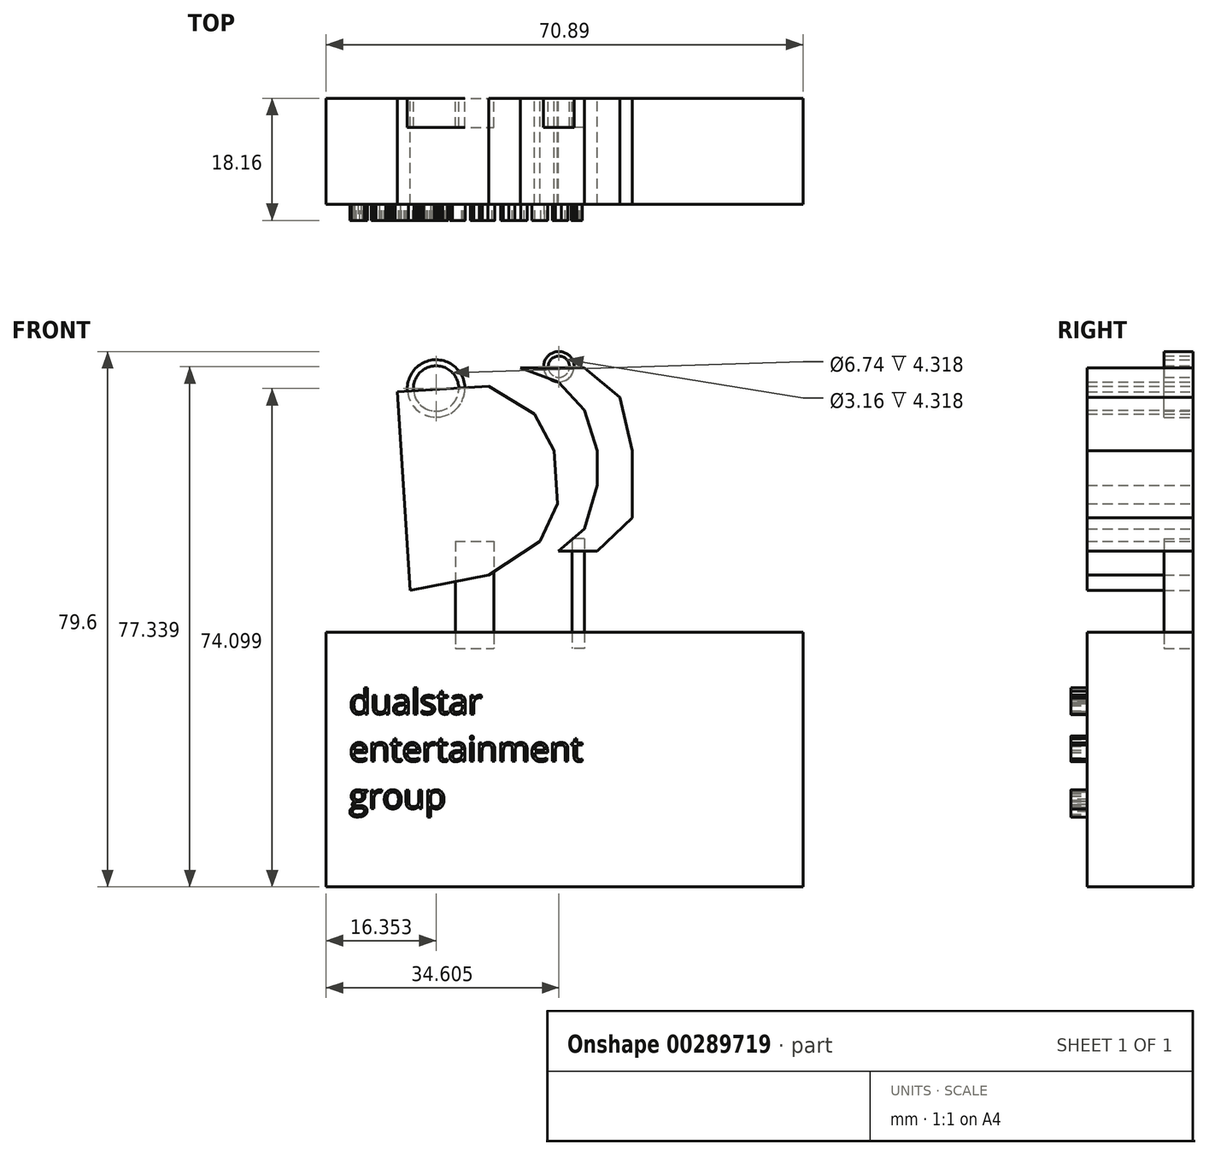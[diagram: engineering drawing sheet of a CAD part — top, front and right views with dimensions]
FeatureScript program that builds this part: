
annotation { "Feature Type Name" : "Feature", "Feature Type Description" : "" }
export const myFeature = defineFeature(function(context is Context, id is Id, definition is map)
    precondition{}
    {
        {
            var Q0;
            Q0=qCreatedBy(makeId("Front.planeOp"),FACE);
            var sketch = newSketch(context, id + "F0", { "sketchPlane" : qUnion([Q0])});
            skLineSegment(sketch, "E0", {"start": v(-25.92, 18.4) * mm, "end": v(-27.8, 47.92) * mm});
            skLineSegment(sketch, "E1", {"start": v(-27.8, 47.92) * mm, "end": v(-14.21, 48.78) * mm});
            skLineSegment(sketch, "E2", {"start": v(-14.21, 48.78) * mm, "end": v(-7.42, 44.6) * mm});
            skLineSegment(sketch, "E3", {"start": v(-7.42, 44.6) * mm, "end": v(-4.5, 39.19) * mm});
            skLineSegment(sketch, "E4", {"start": v(-4.5, 39.19) * mm, "end": v(-4, 31.28) * mm});
            skLineSegment(sketch, "E5", {"start": v(-4, 31.28) * mm, "end": v(-6.59, 25.67) * mm});
            skLineSegment(sketch, "E6", {"start": v(-6.59, 25.67) * mm, "end": v(-14.21, 20.69) * mm});
            skLineSegment(sketch, "E7", {"start": v(-14.21, 20.69) * mm, "end": v(-25.92, 18.4) * mm});
            skLineSegment(sketch, "E8", {"start": v(-9.5, 51.45) * mm, "end": v(-3.88, 49.37) * mm});
            skLineSegment(sketch, "E9", {"start": v(-3.88, 49.37) * mm, "end": v(0, 45.22) * mm});
            skLineSegment(sketch, "E10", {"start": v(0, 45.22) * mm, "end": v(1.94, 39.19) * mm});
            skLineSegment(sketch, "E11", {"start": v(1.94, 39.19) * mm, "end": v(1.94, 34) * mm});
            skLineSegment(sketch, "E12", {"start": v(1.94, 34) * mm, "end": v(0, 27.55) * mm});
            skLineSegment(sketch, "E13", {"start": v(0, 27.55) * mm, "end": v(-3.88, 24.22) * mm});
            skLineSegment(sketch, "E14", {"start": v(-3.88, 24.22) * mm, "end": v(1.94, 24.22) * mm});
            skLineSegment(sketch, "E15", {"start": v(1.94, 24.22) * mm, "end": v(7.14, 29.2) * mm});
            skLineSegment(sketch, "E16", {"start": v(7.14, 29.2) * mm, "end": v(7.14, 34) * mm});
            skLineSegment(sketch, "E17", {"start": v(7.14, 34) * mm, "end": v(7.14, 39.19) * mm});
            skLineSegment(sketch, "E18", {"start": v(7.14, 39.19) * mm, "end": v(5.26, 47.09) * mm});
            skLineSegment(sketch, "E19", {"start": v(5.26, 47.09) * mm, "end": v(0, 51.45) * mm});
            skLineSegment(sketch, "E20", {"start": v(0, 51.45) * mm, "end": v(-9.5, 51.45) * mm});
            skLineSegment(sketch, "E21.bottom", {"start": v(-38.4, 12.16) * mm, "end": v(32.5, 12.16) * mm});
            skLineSegment(sketch, "E21.top", {"start": v(-38.4, -25.68) * mm, "end": v(32.5, -25.68) * mm});
            skLineSegment(sketch, "E21.left", {"start": v(-38.4, 12.16) * mm, "end": v(-38.4, -25.68) * mm});
            skLineSegment(sketch, "E21.right", {"start": v(32.5, 12.16) * mm, "end": v(32.5, -25.68) * mm});
            skSolve(sketch);
        }
        {
            var Q0;
            Q0 = qSketchRegion(id + "F0", true);
            extrude(context, id + "F1", {"entities" : qUnion([Q0]), "depth" : 15.75 * mm});
        }
        {
            var Q0;
            Q0=qCreatedBy(makeId("Front.planeOp"),FACE);
            var sketch = newSketch(context, id + "F2", { "sketchPlane" : qUnion([Q0])});
            skText(sketch, "E22", { "text": "dualstar\nentertainment\ngroup\n", "fontName": "OpenSans-Regular.ttf"});
            const initialGuessF2  = {"E22": [-0.03497, 0, 1, 0, 0.00372]};
            skSetInitialGuess(sketch, initialGuessF2);
            skSolve(sketch);
        }
        {
            var Q0;
            Q0 = qSketchRegion(id + "F2", true);
            extrude(context, id + "F3", {"entities" : qUnion([Q0]), "operationType" : NewBodyOperationType.ADD, "depth" : 18.16 * mm});
        }
        {
            var Q0;
            Q0=qCreatedBy(makeId("Front.planeOp"),FACE);
            var sketch = newSketch(context, id + "F4", { "sketchPlane" : qUnion([Q0])});
            skLineSegment(sketch, "E23.bottom", {"start": v(-19.17, 25.7) * mm, "end": v(-13.46, 25.7) * mm});
            skLineSegment(sketch, "E23.top", {"start": v(-19.17, 9.74) * mm, "end": v(-13.46, 9.74) * mm});
            skLineSegment(sketch, "E23.left", {"start": v(-19.17, 25.7) * mm, "end": v(-19.17, 9.74) * mm});
            skLineSegment(sketch, "E23.right", {"start": v(-13.46, 25.7) * mm, "end": v(-13.46, 9.74) * mm});
            skLineSegment(sketch, "E24.bottom", {"start": v(0, 26.08) * mm, "end": v(-1.85, 26.08) * mm});
            skLineSegment(sketch, "E24.top", {"start": v(0, 9.74) * mm, "end": v(-1.85, 9.74) * mm});
            skLineSegment(sketch, "E24.left", {"start": v(0, 26.08) * mm, "end": v(0, 9.74) * mm});
            skLineSegment(sketch, "E24.right", {"start": v(-1.85, 26.08) * mm, "end": v(-1.85, 9.74) * mm});
            skCircle(sketch, "E25", {"center": v(-22.04, 48.42) * mm, "radius": 4.27 * mm});
            skCircle(sketch, "E26", {"center": v(-22.04, 48.42) * mm, "radius": 3.37 * mm});
            skCircle(sketch, "E27", {"center": v(-3.79, 51.66) * mm, "radius": 2.26 * mm});
            skCircle(sketch, "E28", {"center": v(-3.79, 51.66) * mm, "radius": 1.58 * mm});
            skSolve(sketch);
        }
        {
            var Q0;
            Q0 = qSketchRegion(id + "F4", true);
            extrude(context, id + "F5", {"entities" : qUnion([Q0]), "depth" : 4.32 * mm});
        }
    });
